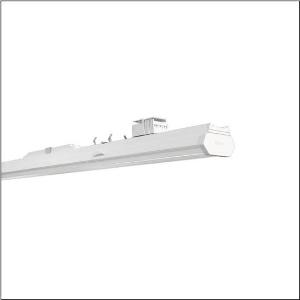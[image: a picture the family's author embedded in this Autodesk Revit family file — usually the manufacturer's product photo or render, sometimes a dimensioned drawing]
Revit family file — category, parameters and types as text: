
# Revit family: licross_r__21_protected_ho_52td1bmn4exm_7a17
name_source: partatom
category: Lighting Fixtures
units: mm (PartAtom-declared; Revit-internal decimal feet)

## family parameters
Cut with Voids When Loaded = No
Host = Face
Light Source = No
Part Type = Normal
Room Calculation Point = No
Round Connector Dimension = Use Diameter
Shared = No

## types (1)
- --- (1 x LED, 14040 lm, 83.2 W, 4000K)
    Apparent Load = 83 VA
    CIE Flux Codes = 54 82 95 97 100
    Color Rendering = 80
    Color Temperature = 4000K
    Default Elevation = 1800 mm
    Description = Licross® 21 Protected HO, luminaire insert, of sheet steel, galvanised, coil coated, white, length: 1.500mm, width: 90mm, height: 103mm, LED rated luminous flux: 14.040lm, light colour: 840, control gear: ON/OFF Multilumen, with plug, 3-pole, with phase selection, mains connection: 220..240V, AC, 50/60Hz, rated input power: 83W, halogen-free wiring, primary optical cover: cover, of PMMA, light emission: direct distribution, primary light characteristic: symmetric, protection rating (complete): IP54, insulation class (complete): insulation class I (protective earthing), certification: CE, ENEC, VDE, UKCA, protection symbol: D if used in an environment with non-conductive dust loads with corresponding accessories, impact resistance: IK06, permissible ambient temperature for indoor applications: -35..+35°C, corresponds to IFS (International Featured Standards) requirements for safety and quality in the food industry, reducing of maximum allowable ambient temperature of 5°C with ceiling mounting, LABS conformity tested according to VDMA 24364:2018-05, packaging unit: 1 piece
    Height = 92 mm
    Lamp = 1 x LED
    Lamp Light Flux = 14040 lm
    Lamp Power = 83.2 W
    Lamp count = 1
    Length = 1500 mm
    Luminous efficacy = 169 lm/W
    Manufacturer = Siteco
    ModVariant = No
    Model = 52TD1BMN4EXM
    Mounting Place = Ceiling
    Mounting Type = Pendant
    Number of Poles = 1
    OnlyDefault = Yes
    Power Factor = 1
    Product Name = Licross® 21 Protected HO
    Product group = luminaire insert
    ProductGroupID = 901
    Protection Class = Protection class I
    Protection Degree = IP 54
    RLX_Detail_Level = 1
    RLX_Emergency_Light_Flux = 0 lm
    RLX_Emergency_Type = 0
    RLX_Emergency_Type_DB = No
    RlxData = <blob elided: 21997 chars, md5=025b9462>
    Socket = socket
    Standby Power = 0 W
    System Light Flux = 14040 lm
    System Power = 83 W
    Type Comments = factory setting: luminous flux: 100 % | (A | C | E) | 195 mA
    Type Image = l_1256148.jpg
    URL = http://relux.com
    VarID = @adj_039335
    Voltage = 0 V
    Weight = 0.00 kg
    Width = 88 mm

## geometry (parser evidence)
native form markers: Blend x4, Sweep x9
no freeform markers — native parametric forms only
